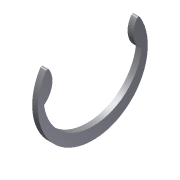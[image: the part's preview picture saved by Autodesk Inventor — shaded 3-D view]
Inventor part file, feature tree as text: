
AUTODESK INVENTOR PART (.ipt)
format: ipt  version: 2013 (Build 170138000, 138)  size: 77,824 bytes
history: native  units: in
note: dims shown in document units (in); Inventor stores cm internally (conversion verified against a paired STEP export)
features: extrude x1, other x1, imported_body x1
ambient origin geometry x8: Origin, YZ Plane, XZ Plane, XY Plane, X Axis, Y Axis, Z Axis, Center Point
feature tree (3):
  extrude  "Extrude1"  [1 undecoded]
  other  "217-2625-019 Rev1_97414A675_grv1"
  imported_body  "Base1"
note: 1 required parameter value undecoded (feature->parameter linkage not recoverable at this tier; creation-order binding heuristic only, values carry confidence <= 0.55)
